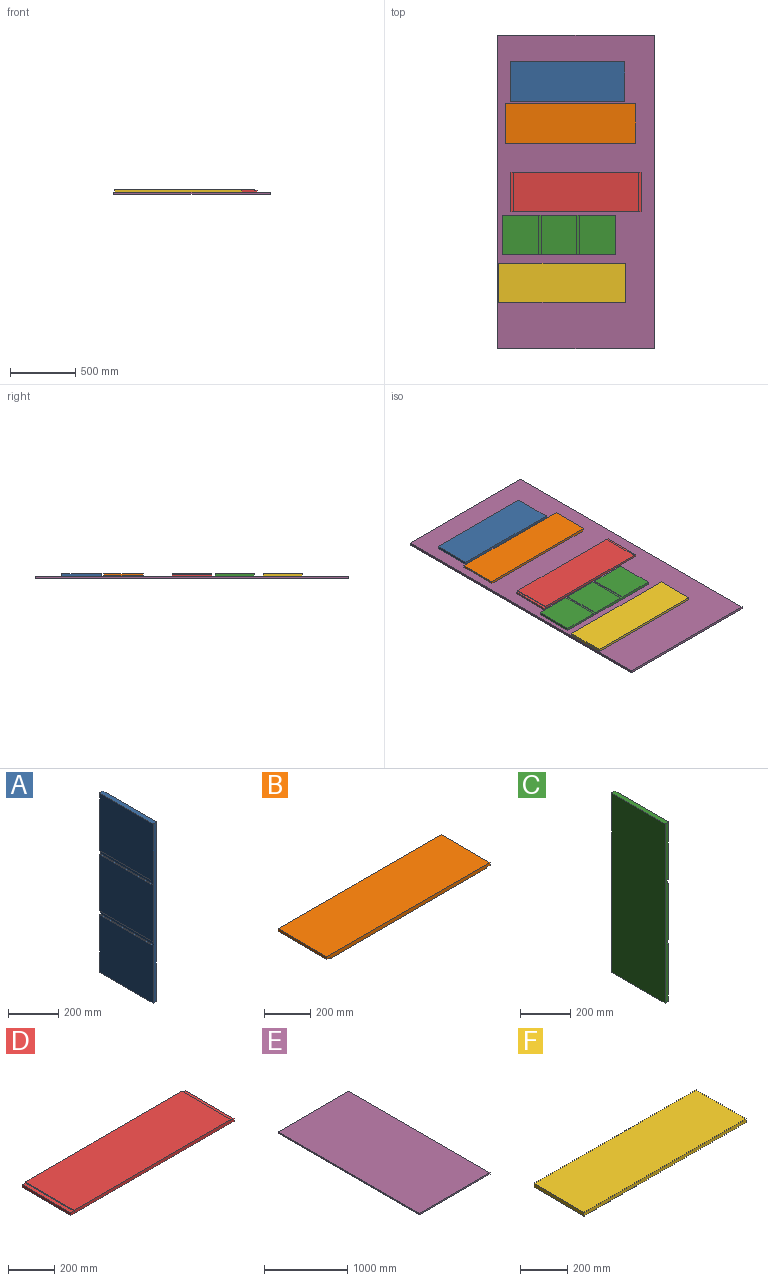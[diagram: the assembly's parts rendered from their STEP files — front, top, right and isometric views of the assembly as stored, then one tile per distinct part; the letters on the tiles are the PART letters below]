
ASSEMBLY  parts=6 mates=5
PART A: 14 faces, bbox 19x300x872 mm
  f0: plane 300x5mm, normal (0,0,1), area 1500mm2, adj f1,f11,f12,f13
  f1: plane 300x274.67mm, normal (-1,0,0), area 82400mm2, adj f0,f2,f12,f13
  f2: plane 300x5mm, normal (0,0,-1), area 1500mm2, adj f1,f3,f12,f13
  f3: plane 300x19mm, normal (-1,0,0), area 5700mm2, adj f2,f4,f12,f13
  f4: plane 300x5mm, normal (0,0,1), area 1500mm2, adj f3,f5,f12,f13
  f5: plane 300x279.67mm, normal (-1,0,0), area 83900mm2, adj f4,f6,f12,f13
  f6: plane 300x19mm, normal (0,0,-1), area 5700mm2, adj f5,f7,f12,f13
  f7: plane 872x300mm, normal (1,0,0), area 261600mm2, adj f6,f8,f12,f13
  f8: plane 300x19mm, normal (0,0,1), area 5700mm2, adj f7,f9,f12,f13
  f9: plane 300x279.67mm, normal (-1,0,0), area 83900mm2, adj f8,f10,f12,f13
  f10: plane 300x5mm, normal (0,0,-1), area 1500mm2, adj f9,f11,f12,f13
  f11: plane 300x19mm, normal (-1,0,0), area 5700mm2, adj f0,f10,f12,f13
  f12: plane 872x19mm, normal (0,1,0), area 16378mm2, adj f0,f1,f2,f3,f4,f5,f6,f7
  f13: plane 872x19mm, normal (0,-1,0), area 16378mm2, adj f0,f1,f2,f3,f4,f5,f6,f7
PART B: 10 faces, bbox 1000x300x19 mm
  f0: plane 300x14mm, normal (-1,0,0), area 4200mm2, adj f1,f7,f8,f9
  f1: plane 300x19mm, normal (0,0,-1), area 5700mm2, adj f0,f2,f8,f9
  f2: plane 300x5mm, normal (-1,0,0), area 1500mm2, adj f1,f3,f8,f9
  f3: plane 962x300mm, normal (0,0,-1), area 288600mm2, adj f2,f4,f8,f9
  f4: plane 300x5mm, normal (1,0,0), area 1500mm2, adj f3,f5,f8,f9
  f5: plane 300x19mm, normal (0,0,-1), area 5700mm2, adj f4,f6,f8,f9
  f6: plane 300x14mm, normal (1,0,0), area 4200mm2, adj f5,f7,f8,f9
  f7: plane 1000x300mm, normal (0,0,1), area 300000mm2, adj f0,f6,f8,f9
  f8: plane 1000x19mm, normal (0,1,0), area 18810mm2, adj f0,f1,f2,f3,f4,f5,f6,f7
  f9: plane 1000x19mm, normal (0,-1,0), area 18810mm2, adj f0,f1,f2,f3,f4,f5,f6,f7
PART C: 14 faces, bbox 19x300x872 mm
  f0: plane 300x274.67mm, normal (1,0,0), area 82400mm2, adj f1,f11,f12,f13
  f1: plane 300x5mm, normal (0,0,1), area 1500mm2, adj f0,f2,f12,f13
  f2: plane 300x19mm, normal (1,0,0), area 5700mm2, adj f1,f3,f12,f13
  f3: plane 300x5mm, normal (0,0,-1), area 1500mm2, adj f2,f4,f12,f13
  f4: plane 300x279.67mm, normal (1,0,0), area 83900mm2, adj f3,f5,f12,f13
  f5: plane 300x19mm, normal (0,0,1), area 5700mm2, adj f4,f6,f12,f13
  f6: plane 872x300mm, normal (-1,0,0), area 261600mm2, adj f5,f7,f12,f13
  f7: plane 300x19mm, normal (0,0,-1), area 5700mm2, adj f6,f8,f12,f13
  f8: plane 300x279.67mm, normal (1,0,0), area 83900mm2, adj f7,f9,f12,f13
  f9: plane 300x5mm, normal (0,0,1), area 1500mm2, adj f8,f10,f12,f13
  f10: plane 300x19mm, normal (1,0,0), area 5700mm2, adj f9,f11,f12,f13
  f11: plane 300x5mm, normal (0,0,-1), area 1500mm2, adj f0,f10,f12,f13
  f12: plane 872x19mm, normal (0,1,0), area 16378mm2, adj f0,f1,f2,f3,f4,f5,f6,f7
  f13: plane 872x19mm, normal (0,-1,0), area 16378mm2, adj f0,f1,f2,f3,f4,f5,f6,f7
PART D: 10 faces, bbox 1000x300x19 mm
  f0: plane 300x14mm, normal (-1,0,0), area 4200mm2, adj f1,f7,f8,f9
  f1: plane 1000x300mm, normal (0,0,-1), area 300000mm2, adj f0,f2,f8,f9
  f2: plane 300x14mm, normal (1,0,0), area 4200mm2, adj f1,f3,f8,f9
  f3: plane 300x19mm, normal (0,0,1), area 5700mm2, adj f2,f4,f8,f9
  f4: plane 300x5mm, normal (1,0,0), area 1500mm2, adj f3,f5,f8,f9
  f5: plane 962x300mm, normal (0,0,1), area 288600mm2, adj f4,f6,f8,f9
  f6: plane 300x5mm, normal (-1,0,0), area 1500mm2, adj f5,f7,f8,f9
  f7: plane 300x19mm, normal (0,0,1), area 5700mm2, adj f0,f6,f8,f9
  f8: plane 1000x19mm, normal (0,1,0), area 18810mm2, adj f0,f1,f2,f3,f4,f5,f6,f7
  f9: plane 1000x19mm, normal (0,-1,0), area 18810mm2, adj f0,f1,f2,f3,f4,f5,f6,f7
PART E: 6 faces, bbox 1200x2400x19 mm
  f0: plane 2400x19mm, normal (-1,0,0), area 45600mm2, adj f1,f3,f4,f5
  f1: plane 1200x19mm, normal (0,-1,0), area 22800mm2, adj f0,f2,f4,f5
  f2: plane 2400x19mm, normal (1,0,0), area 45600mm2, adj f1,f3,f4,f5
  f3: plane 1200x19mm, normal (0,1,0), area 22800mm2, adj f0,f2,f4,f5
  f4: plane 2400x1200mm, normal (0,0,1), area 2880000mm2, adj f0,f1,f2,f3
  f5: plane 2400x1200mm, normal (0,0,-1), area 2880000mm2, adj f0,f1,f2,f3
PART F: 6 faces, bbox 972x300x19 mm
  f0: plane 972x300mm, normal (0,0,1), area 291600mm2, adj f1,f3,f4,f5
  f1: plane 300x19mm, normal (-1,0,0), area 5700mm2, adj f0,f2,f4,f5
  f2: plane 972x300mm, normal (0,0,-1), area 291600mm2, adj f1,f3,f4,f5
  f3: plane 300x19mm, normal (1,0,0), area 5700mm2, adj f0,f2,f4,f5
  f4: plane 972x19mm, normal (0,1,0), area 18468mm2, adj f0,f1,f2,f3
  f5: plane 972x19mm, normal (0,-1,0), area 18468mm2, adj f0,f1,f2,f3
PLACE A rot(axis=(0,-1,0),90deg) t=(987.39,1896.97,-596.93)mm
PLACE B t=(59.96,1575.16,-496.93)mm
PLACE C rot(axis=(0,-1,0),90deg) t=(919.59,722.57,384.07)mm
PLACE D rot(axis=(0,1,0),0deg) t=(100,1050,384.07)mm
PLACE E t=(0,0,365.07)mm
PLACE F rot(axis=(0,1,0),0deg) t=(-6.44,354.61,-203.26)mm
MATE planar C.f0 <-> B.f7  axis (0,0,1) through (469.59,872.57,403.07)mm
MATE planar F.f0 <-> C.f0  axis (0,0,1) through (493.56,504.61,403.07)mm
MATE planar D.f5 <-> C.f0  axis (0,0,1) through (600,1200,403.07)mm
MATE planar B.f3 <-> E.f4  axis (0,0,-1) through (559.96,1725.16,384.07)mm
MATE planar A.f7 <-> B.f7  axis (0,0,1) through (537.39,2046.97,403.07)mm
